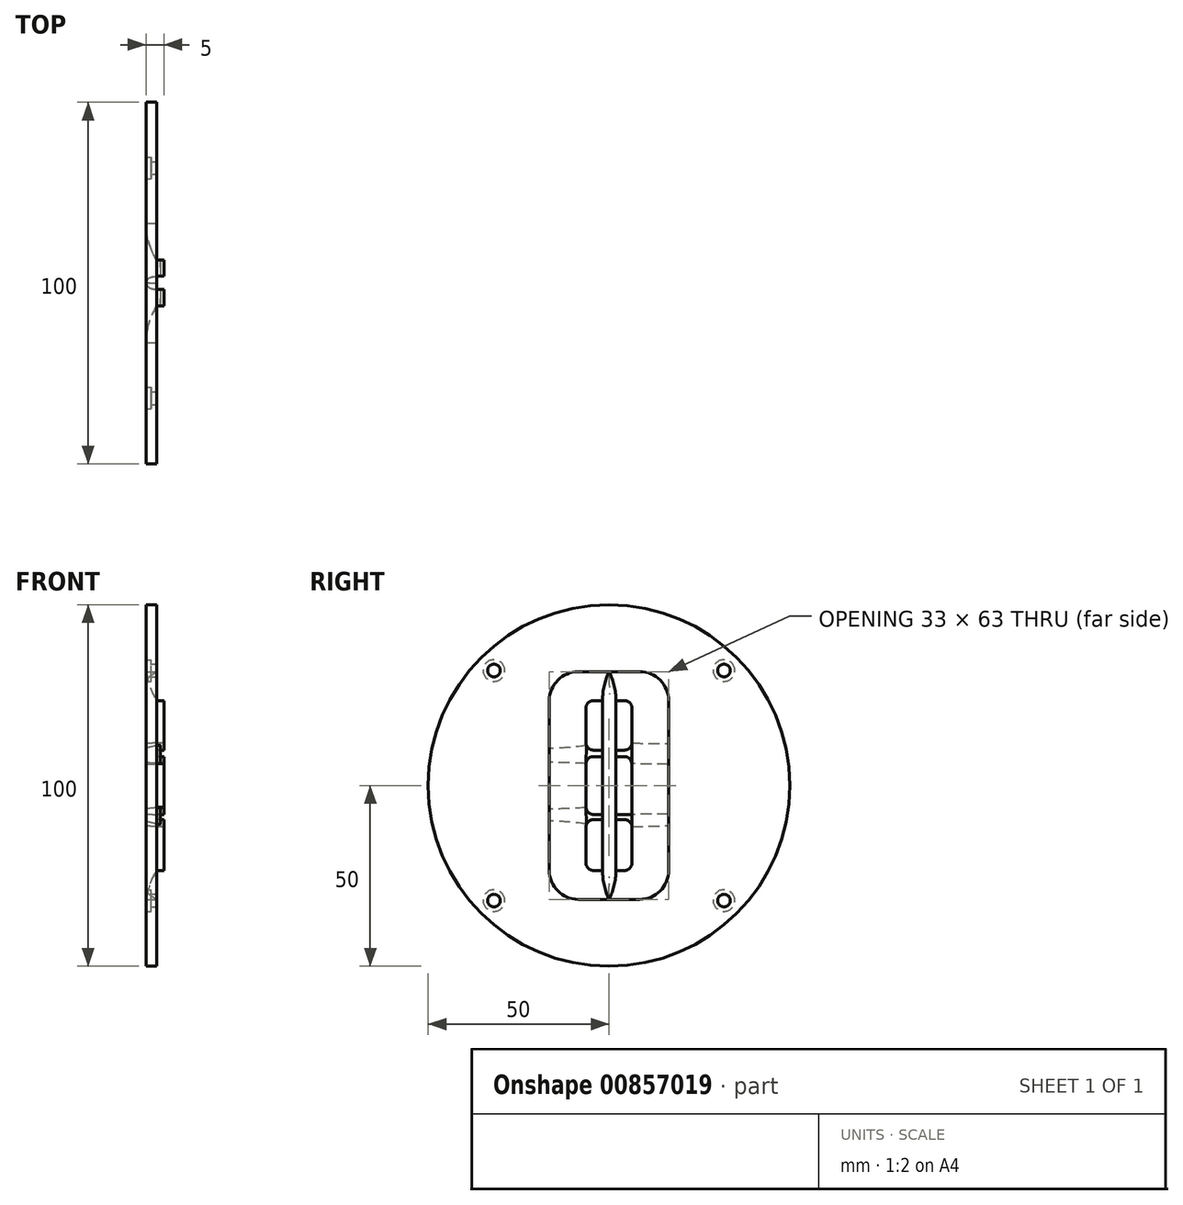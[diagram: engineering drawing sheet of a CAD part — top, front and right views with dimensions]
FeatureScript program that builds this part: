
annotation { "Feature Type Name" : "Feature", "Feature Type Description" : "" }
export const myFeature = defineFeature(function(context is Context, id is Id, definition is map)
    precondition{}
    {
        {
            var Q0;
            Q0=qCreatedBy(makeId("Right.planeOp"),FACE);
            var sketch = newSketch(context, id + "F0", { "sketchPlane" : qUnion([Q0])});
            skCircle(sketch, "E0", {"center": v(0, 0) * mm, "radius": 45 * mm});
            skCircle(sketch, "E1", {"center": v(0, 0) * mm, "radius": 50 * mm});
            skLineSegment(sketch, "E2", {"start": v(0, 0) * mm, "end": v(0, 58.72) * mm});
            skCircle(sketch, "E3", {"center": v(31.82, 31.82) * mm, "radius": 1.75 * mm});
            skCircle(sketch, "E4", {"center": v(31.82, 31.82) * mm, "radius": 3 * mm});
            skCircle(sketch, "E5.1.0", {"center": v(-31.82, 31.82) * mm, "radius": 3 * mm});
            skCircle(sketch, "E5.2.0", {"center": v(-31.82, -31.82) * mm, "radius": 3 * mm});
            skCircle(sketch, "E5.3.0", {"center": v(31.82, -31.82) * mm, "radius": 3 * mm});
            skCircle(sketch, "E6.1.0", {"center": v(-31.82, 31.82) * mm, "radius": 1.75 * mm});
            skCircle(sketch, "E6.2.0", {"center": v(-31.82, -31.82) * mm, "radius": 1.75 * mm});
            skCircle(sketch, "E6.3.0", {"center": v(31.82, -31.82) * mm, "radius": 1.75 * mm});
            skLineSegment(sketch, "E7", {"start": v(0, 0) * mm, "end": v(0, -59.24) * mm});
            skLineSegment(sketch, "E8.bottom", {"start": v(8.5, 31.5) * mm, "end": v(-8.5, 31.5) * mm});
            skLineSegment(sketch, "E8.top", {"start": v(8.5, -31.5) * mm, "end": v(-8.5, -31.5) * mm});
            skLineSegment(sketch, "E8.left", {"start": v(16.5, 23.5) * mm, "end": v(16.5, -23.5) * mm});
            skLineSegment(sketch, "E8.right", {"start": v(-16.5, 23.5) * mm, "end": v(-16.5, -23.5) * mm});
            skLineSegment(sketch, "E9.bottom", {"start": v(4.28, 8) * mm, "end": v(2.98, 8) * mm});
            skLineSegment(sketch, "E9.top", {"start": v(6.28, -8) * mm, "end": v(2.98, -8) * mm});
            skLineSegment(sketch, "E9.left", {"start": v(6.28, 6) * mm, "end": v(6.28, -8) * mm});
            skLineSegment(sketch, "E10.trimOffspring", {"start": v(29.7, 29.7) * mm, "end": v(45.9, 45.9) * mm});
            skPoint(sketch, "E11.orphan", {"position": v(2.98, -17) * mm});
            skPoint(sketch, "E12.visualSharp", {"position": v(16.5, 31.5) * mm});
            skArc(sketch, "E12.filletArc", {"start": v(16.5, 23.5) * mm, "mid": v(14.16, 29.16) * mm, "end": v(8.5, 31.5) * mm});
            skPoint(sketch, "E13.visualSharp", {"position": v(-16.5, -31.5) * mm});
            skArc(sketch, "E13.filletArc", {"start": v(-16.5, -23.5) * mm, "mid": v(-14.16, -29.16) * mm, "end": v(-8.5, -31.5) * mm});
            skPoint(sketch, "E14.visualSharp", {"position": v(-16.5, 31.5) * mm});
            skArc(sketch, "E14.filletArc", {"start": v(-8.5, 31.5) * mm, "mid": v(-14.16, 29.16) * mm, "end": v(-16.5, 23.5) * mm});
            skPoint(sketch, "E15.visualSharp", {"position": v(16.5, -31.5) * mm});
            skArc(sketch, "E15.filletArc", {"start": v(8.5, -31.5) * mm, "mid": v(14.16, -29.16) * mm, "end": v(16.5, -23.5) * mm});
            skLineSegment(sketch, "E16.bottom", {"start": v(4.35, 23.5) * mm, "end": v(1.93, 23.5) * mm});
            skLineSegment(sketch, "E16.top", {"start": v(4.35, -23.5) * mm, "end": v(1.93, -23.5) * mm});
            skLineSegment(sketch, "E16.left", {"start": v(6.35, 21.5) * mm, "end": v(6.35, 11.8) * mm});
            skLineSegment(sketch, "E16.right", {"start": v(-6.35, 21.5) * mm, "end": v(-6.35, 11.8) * mm});
            skLineSegment(sketch, "E17", {"start": v(1.93, 23.5) * mm, "end": v(1.93, -23.5) * mm});
            skLineSegment(sketch, "E18", {"start": v(-1.78, -23.5) * mm, "end": v(-1.78, 23.5) * mm});
            skLineSegment(sketch, "E19", {"start": v(4.35, 9.8) * mm, "end": v(1.93, 9.8) * mm});
            skLineSegment(sketch, "E20", {"start": v(2.98, 8) * mm, "end": v(1.93, 8) * mm});
            skLineSegment(sketch, "E21", {"start": v(6.28, -8) * mm, "end": v(1.93, -8) * mm});
            skLineSegment(sketch, "E22", {"start": v(4.35, -9.47) * mm, "end": v(1.93, -9.47) * mm});
            skArc(sketch, "E23", {"start": v(1.93, 23.5) * mm, "mid": v(1.44, 27.61) * mm, "end": v(0, 31.5) * mm});
            skArc(sketch, "E24", {"start": v(0, 31.5) * mm, "mid": v(-1.33, 27.6) * mm, "end": v(-1.78, 23.5) * mm});
            skArc(sketch, "E25", {"start": v(-1.78, -23.5) * mm, "mid": v(-1.33, -27.6) * mm, "end": v(0, -31.5) * mm});
            skArc(sketch, "E26", {"start": v(0, -31.5) * mm, "mid": v(1.44, -27.61) * mm, "end": v(1.93, -23.5) * mm});
            skPoint(sketch, "E27.visualSharp", {"position": v(6.35, -23.5) * mm});
            skArc(sketch, "E27.filletArc", {"start": v(4.35, -23.5) * mm, "mid": v(5.76, -22.91) * mm, "end": v(6.35, -21.5) * mm});
            skPoint(sketch, "E28.visualSharp", {"position": v(-6.35, -23.5) * mm});
            skArc(sketch, "E28.filletArc", {"start": v(-6.35, -21.5) * mm, "mid": v(-5.76, -22.91) * mm, "end": v(-4.35, -23.5) * mm});
            skPoint(sketch, "E29.visualSharp", {"position": v(-6.35, 23.5) * mm});
            skArc(sketch, "E29.filletArc", {"start": v(-4.35, 23.5) * mm, "mid": v(-5.76, 22.91) * mm, "end": v(-6.35, 21.5) * mm});
            skPoint(sketch, "E30.visualSharp", {"position": v(6.35, 23.5) * mm});
            skArc(sketch, "E30.filletArc", {"start": v(6.35, 21.5) * mm, "mid": v(5.76, 22.91) * mm, "end": v(4.35, 23.5) * mm});
            skLineSegment(sketch, "E31.trimOffspring", {"start": v(-6.35, 6) * mm, "end": v(-6.35, -6) * mm});
            skLineSegment(sketch, "E32.trimOffspring", {"start": v(-1.78, 8) * mm, "end": v(-4.35, 8) * mm});
            skLineSegment(sketch, "E33.trimOffspring", {"start": v(-1.78, 9.8) * mm, "end": v(-4.35, 9.8) * mm});
            skLineSegment(sketch, "E34.trimOffspring", {"start": v(6.35, -11.47) * mm, "end": v(6.35, -21.5) * mm});
            skLineSegment(sketch, "E35.trimOffspring", {"start": v(-1.78, 23.5) * mm, "end": v(-4.35, 23.5) * mm});
            skLineSegment(sketch, "E36.trimOffspring", {"start": v(-6.35, -11.47) * mm, "end": v(-6.35, -21.5) * mm});
            skLineSegment(sketch, "E37.trimOffspring", {"start": v(-1.78, -8) * mm, "end": v(-4.35, -8) * mm});
            skLineSegment(sketch, "E38.trimOffspring", {"start": v(-1.78, -9.47) * mm, "end": v(-4.35, -9.47) * mm});
            skLineSegment(sketch, "E39.trimOffspring", {"start": v(-1.78, -23.5) * mm, "end": v(-4.35, -23.5) * mm});
            skPoint(sketch, "E40.visualSharp", {"position": v(6.35, -9.47) * mm});
            skArc(sketch, "E40.filletArc", {"start": v(6.35, -11.47) * mm, "mid": v(5.76, -10.05) * mm, "end": v(4.35, -9.47) * mm});
            skPoint(sketch, "E41.visualSharp", {"position": v(6.28, 8) * mm});
            skArc(sketch, "E41.filletArc", {"start": v(6.28, 6) * mm, "mid": v(5.7, 7.41) * mm, "end": v(4.28, 8) * mm});
            skPoint(sketch, "E42.visualSharp", {"position": v(-6.35, 8) * mm});
            skArc(sketch, "E42.filletArc", {"start": v(-4.35, 8) * mm, "mid": v(-5.76, 7.41) * mm, "end": v(-6.35, 6) * mm});
            skPoint(sketch, "E43.visualSharp", {"position": v(6.35, 9.8) * mm});
            skArc(sketch, "E43.filletArc", {"start": v(4.35, 9.8) * mm, "mid": v(5.76, 10.39) * mm, "end": v(6.35, 11.8) * mm});
            skPoint(sketch, "E44.visualSharp", {"position": v(-6.35, 9.8) * mm});
            skArc(sketch, "E44.filletArc", {"start": v(-6.35, 11.8) * mm, "mid": v(-5.76, 10.39) * mm, "end": v(-4.35, 9.8) * mm});
            skPoint(sketch, "E45.visualSharp", {"position": v(-6.35, -9.47) * mm});
            skArc(sketch, "E45.filletArc", {"start": v(-4.35, -9.47) * mm, "mid": v(-5.76, -10.05) * mm, "end": v(-6.35, -11.47) * mm});
            skPoint(sketch, "E46.visualSharp", {"position": v(-6.35, -8) * mm});
            skArc(sketch, "E46.filletArc", {"start": v(-6.35, -6) * mm, "mid": v(-5.76, -7.41) * mm, "end": v(-4.35, -8) * mm});
            skLineSegment(sketch, "E47", {"start": v(6.35, 11.8) * mm, "end": v(6.28, 6) * mm});
            skLineSegment(sketch, "E48", {"start": v(-6.22, 11.09) * mm, "end": v(-6.35, 6) * mm});
            skLineSegment(sketch, "E49", {"start": v(6.28, -8) * mm, "end": v(6.35, -11.47) * mm});
            skLineSegment(sketch, "E50", {"start": v(-6.35, -6) * mm, "end": v(-6.2, -10.68) * mm});
            skSolve(sketch);
        }
        {
            var Q0;
            {var subQ0=sQuery(id+"F0.wireOp",EDGE,"E4");var subQ1=sQuery(id+"F0.wireOp",EDGE,"E0");var subQ2=makeQuery(id+"F0.imprint","INTERSECT",VERTEX,{"disambiguationData":[OD(1.0)],"derivedFrom":[subQ1,subQ0]});Q0=makeQuery(id+"F0.imprint","IMPRINT",FACE,{"disambiguationData":[TD([[makeQuery(id+"F0.imprint","IMPRINT",EDGE,{"disambiguationData":[TD([[subQ2,-1.0]])],"derivedFrom":subQ1}),-1.0]])]});}
            var Q1;
            {var subQ1=sQuery(id+"F0.wireOp",EDGE,"E0");var subQ7=sQuery(id+"F0.wireOp",EDGE,"E7");var subQ11=makeQuery(id+"F0.imprint","INTERSECT",VERTEX,{"derivedFrom":[subQ1,subQ7]});Q1=makeQuery(id+"F0.imprint","IMPRINT",FACE,{"disambiguationData":[TD([[makeQuery(id+"F0.imprint","IMPRINT",EDGE,{"disambiguationData":[TD([[subQ11,-1.0]])],"derivedFrom":subQ1}),-1.0]])]});}
            var Q2;
            Q2=makeQuery(id+"F0.imprint","IMPRINT",FACE,{"disambiguationData":[TD([[makeQuery(id+"F0.imprint","IMPRINT",EDGE,{"derivedFrom":sQuery(id+"F0.wireOp",EDGE,"E8.left")}),1.0]])]});
            var Q3;
            {var subQ1=sQuery(id+"F0.wireOp",EDGE,"E0");var subQ5=sQuery(id+"F0.wireOp",EDGE,"E2");var subQ8=makeQuery(id+"F0.imprint","INTERSECT",VERTEX,{"derivedFrom":[subQ1,subQ5]});Q3=makeQuery(id+"F0.imprint","IMPRINT",FACE,{"disambiguationData":[TD([[makeQuery(id+"F0.imprint","IMPRINT",EDGE,{"disambiguationData":[TD([[subQ8,-1.0]])],"derivedFrom":subQ1}),-1.0]])]});}
            var Q4;
            Q4=makeQuery(id+"F0.imprint","IMPRINT",FACE,{"disambiguationData":[TD([[makeQuery(id+"F0.imprint","IMPRINT",EDGE,{"derivedFrom":sQuery(id+"F0.wireOp",EDGE,"E8.right")}),-1.0]])]});
            extrude(context, id + "F1", {"entities" : qUnion([Q0, Q1, Q2, Q3, Q4]), "oppositeDirection" : true, "depth" : 3 * mm, "offsetDistance" : 25 * mm});
        }
        {
            var Q0;
            Q0=makeQuery(id+"F0.imprint","IMPRINT",FACE,{"disambiguationData":[TD([[makeQuery(id+"F0.imprint","IMPRINT",EDGE,{"derivedFrom":sQuery(id+"F0.wireOp",EDGE,"E9.bottom")}),-1.0]])]});
            var Q1;
            {var subQ1=sQuery(id+"F0.wireOp",EDGE,"E32.trimOffspring");Q1=makeQuery(id+"F0.imprint","IMPRINT",FACE,{"disambiguationData":[TD([[makeQuery(id+"F0.imprint","IMPRINT",EDGE,{"derivedFrom":subQ1}),-1.0]])]});}
            var Q2;
            {var subQ4=sQuery(id+"F0.wireOp",EDGE,"E37.trimOffspring");Q2=makeQuery(id+"F0.imprint","IMPRINT",FACE,{"disambiguationData":[TD([[makeQuery(id+"F0.imprint","IMPRINT",EDGE,{"derivedFrom":subQ4}),1.0]])]});}
            var Q3;
            {var subQ0=sQuery(id+"F0.wireOp",EDGE,"E22");Q3=makeQuery(id+"F0.imprint","IMPRINT",FACE,{"disambiguationData":[TD([[makeQuery(id+"F0.imprint","IMPRINT",EDGE,{"derivedFrom":subQ0}),-1.0]])]});}
            extrude(context, id + "F2", {"entities" : qUnion([Q0, Q1, Q2, Q3]), "depth" : 1 * mm, "offsetDistance" : 25 * mm});
        }
        {
            var Q0;
            {var subQ0=sQuery(id+"F0.wireOp",EDGE,"E23");Q0=makeQuery(id+"F0.imprint","IMPRINT",FACE,{"disambiguationData":[TD([[makeQuery(id+"F0.imprint","IMPRINT",EDGE,{"derivedFrom":subQ0}),1.0]])]});}
            var Q1;
            {var subQ3=sQuery(id+"F0.wireOp",EDGE,"E24");Q1=makeQuery(id+"F0.imprint","IMPRINT",FACE,{"disambiguationData":[TD([[makeQuery(id+"F0.imprint","IMPRINT",EDGE,{"derivedFrom":subQ3}),1.0]])]});}
            extrude(context, id + "F3", {"entities" : qUnion([Q0, Q1]), "oppositeDirection" : true, "depth" : 3 * mm, "offsetDistance" : 25 * mm, "hasDraft" : true, "draftAngle" : 15 * degree, "draftPullDirection" : true});
        }
        {
            var Q0;
            Q0=makeQuery(id+"F3.opExtrude","CAP_EDGE",EDGE,{"disambiguationData":[OSD([sQuery(id+"F0.wireOp",EDGE,"E17")])],"isStart":false});
            var Q1;
            Q1=makeQuery(id+"F3.opExtrude","CAP_EDGE",EDGE,{"disambiguationData":[OSD([sQuery(id+"F0.wireOp",EDGE,"E18")])],"isStart":false});
            fillet(context, id + "F4", {"entities" : qUnion([Q0, Q1]), "radius" : 1.25 * mm, "tangentPropagation" : true, "allowEdgeOverflow" : false});
        }
        {
            var Q0;
            Q0=makeQuery(id+"F0.imprint","IMPRINT",FACE,{"disambiguationData":[TD([[makeQuery(id+"F0.imprint","IMPRINT",EDGE,{"derivedFrom":sQuery(id+"F0.wireOp",EDGE,"E8.left")}),-1.0]])]});
            var Q1;
            Q1=makeQuery(id+"F0.imprint","IMPRINT",FACE,{"disambiguationData":[TD([[makeQuery(id+"F0.imprint","IMPRINT",EDGE,{"derivedFrom":sQuery(id+"F0.wireOp",EDGE,"E8.right")}),1.0]])]});
            extrude(context, id + "F5", {"entities" : qUnion([Q0, Q1]), "oppositeDirection" : true, "depth" : 3 * mm, "offsetDistance" : 25 * mm});
        }
        {
            var Q0;
            Q0=makeQuery(id+"F5.opExtrude","CAP_EDGE",EDGE,{"disambiguationData":[OSD([sQuery(id+"F0.wireOp",EDGE,"E31.trimOffspring")])],"isStart":false});
            var Q1;
            Q1=makeQuery(id+"F5.opExtrude","CAP_EDGE",EDGE,{"disambiguationData":[OSD([sQuery(id+"F0.wireOp",EDGE,"E36.trimOffspring")])],"isStart":false});
            var Q2;
            Q2=makeQuery(id+"F5.opExtrude","CAP_EDGE",EDGE,{"disambiguationData":[OSD([sQuery(id+"F0.wireOp",EDGE,"E16.right")])],"isStart":false});
            var Q3;
            Q3=makeQuery(id+"F5.opExtrude","CAP_EDGE",EDGE,{"disambiguationData":[OSD([sQuery(id+"F0.wireOp",EDGE,"E9.left")])],"isStart":false});
            var Q4;
            Q4=makeQuery(id+"F5.opExtrude","CAP_EDGE",EDGE,{"disambiguationData":[OSD([sQuery(id+"F0.wireOp",EDGE,"E16.left")])],"isStart":false});
            var Q5;
            Q5=makeQuery(id+"F5.opExtrude","CAP_EDGE",EDGE,{"disambiguationData":[OSD([sQuery(id+"F0.wireOp",EDGE,"E34.trimOffspring")])],"isStart":false});
            fillet(context, id + "F6", {"entities" : qUnion([Q0, Q1, Q2, Q3, Q4, Q5]), "radius" : 18.5 * mm, "tangentPropagation" : true, "allowEdgeOverflow" : false});
        }
        {
            var Q0;
            Q0=qSketchRegion(id+"F0",true);
            var Q1;
            {var subQ0=sQuery(id+"F0.wireOp",EDGE,"E5.1.0");var subQ1=sQuery(id+"F0.wireOp",EDGE,"E0");var subQ2=makeQuery(id+"F0.imprint","INTERSECT",VERTEX,{"disambiguationData":[OD(0.0)],"derivedFrom":[subQ1,subQ0]});Q1=makeQuery(id+"F0.imprint","IMPRINT",FACE,{"disambiguationData":[TD([[makeQuery(id+"F0.imprint","IMPRINT",EDGE,{"disambiguationData":[TD([[subQ2,-1.0]])],"derivedFrom":subQ1}),1.0]])]});}
            var Q2;
            {var subQ0=sQuery(id+"F0.wireOp",EDGE,"E5.2.0");var subQ1=sQuery(id+"F0.wireOp",EDGE,"E0");var subQ2=makeQuery(id+"F0.imprint","INTERSECT",VERTEX,{"disambiguationData":[OD(0.0)],"derivedFrom":[subQ1,subQ0]});Q2=makeQuery(id+"F0.imprint","IMPRINT",FACE,{"disambiguationData":[TD([[makeQuery(id+"F0.imprint","IMPRINT",EDGE,{"disambiguationData":[TD([[subQ2,-1.0]])],"derivedFrom":subQ1}),-1.0]])]});}
            var Q3;
            {var subQ0=sQuery(id+"F0.wireOp",EDGE,"E5.2.0");var subQ1=sQuery(id+"F0.wireOp",EDGE,"E0");var subQ2=makeQuery(id+"F0.imprint","INTERSECT",VERTEX,{"disambiguationData":[OD(0.0)],"derivedFrom":[subQ1,subQ0]});Q3=makeQuery(id+"F0.imprint","IMPRINT",FACE,{"disambiguationData":[TD([[makeQuery(id+"F0.imprint","IMPRINT",EDGE,{"disambiguationData":[TD([[subQ2,-1.0]])],"derivedFrom":subQ1}),1.0]])]});}
            var Q4;
            {var subQ0=sQuery(id+"F0.wireOp",EDGE,"E5.3.0");var subQ1=sQuery(id+"F0.wireOp",EDGE,"E0");var subQ2=makeQuery(id+"F0.imprint","INTERSECT",VERTEX,{"disambiguationData":[OD(0.0)],"derivedFrom":[subQ1,subQ0]});Q4=makeQuery(id+"F0.imprint","IMPRINT",FACE,{"disambiguationData":[TD([[makeQuery(id+"F0.imprint","IMPRINT",EDGE,{"disambiguationData":[TD([[subQ2,-1.0]])],"derivedFrom":subQ1}),-1.0]])]});}
            var Q5;
            {var subQ0=sQuery(id+"F0.wireOp",EDGE,"E5.3.0");var subQ1=sQuery(id+"F0.wireOp",EDGE,"E0");var subQ2=makeQuery(id+"F0.imprint","INTERSECT",VERTEX,{"disambiguationData":[OD(0.0)],"derivedFrom":[subQ1,subQ0]});Q5=makeQuery(id+"F0.imprint","IMPRINT",FACE,{"disambiguationData":[TD([[makeQuery(id+"F0.imprint","IMPRINT",EDGE,{"disambiguationData":[TD([[subQ2,-1.0]])],"derivedFrom":subQ1}),1.0]])]});}
            var Q6;
            {var subQ0=sQuery(id+"F0.wireOp",EDGE,"E3");var subQ1=sQuery(id+"F0.wireOp",EDGE,"E0");var subQ2=makeQuery(id+"F0.imprint","INTERSECT",VERTEX,{"disambiguationData":[OD(0.0)],"derivedFrom":[subQ1,subQ0]});Q6=makeQuery(id+"F0.imprint","IMPRINT",FACE,{"disambiguationData":[TD([[makeQuery(id+"F0.imprint","IMPRINT",EDGE,{"disambiguationData":[TD([[subQ2,1.0]])],"derivedFrom":subQ1}),1.0]])]});}
            var Q7;
            {var subQ0=sQuery(id+"F0.wireOp",EDGE,"E3");var subQ1=sQuery(id+"F0.wireOp",EDGE,"E0");var subQ2=makeQuery(id+"F0.imprint","INTERSECT",VERTEX,{"disambiguationData":[OD(1.0)],"derivedFrom":[subQ1,subQ0]});Q7=makeQuery(id+"F0.imprint","IMPRINT",FACE,{"disambiguationData":[TD([[makeQuery(id+"F0.imprint","IMPRINT",EDGE,{"disambiguationData":[TD([[subQ2,-1.0]])],"derivedFrom":subQ1}),1.0]])]});}
            var Q8;
            {var subQ0=sQuery(id+"F0.wireOp",EDGE,"E3");var subQ1=sQuery(id+"F0.wireOp",EDGE,"E0");var subQ2=makeQuery(id+"F0.imprint","INTERSECT",VERTEX,{"disambiguationData":[OD(1.0)],"derivedFrom":[subQ1,subQ0]});Q8=makeQuery(id+"F0.imprint","IMPRINT",FACE,{"disambiguationData":[TD([[makeQuery(id+"F0.imprint","IMPRINT",EDGE,{"disambiguationData":[TD([[subQ2,-1.0]])],"derivedFrom":subQ1}),-1.0]])]});}
            var Q9;
            {var subQ0=sQuery(id+"F0.wireOp",EDGE,"E3");var subQ1=sQuery(id+"F0.wireOp",EDGE,"E0");var subQ2=makeQuery(id+"F0.imprint","INTERSECT",VERTEX,{"disambiguationData":[OD(0.0)],"derivedFrom":[subQ1,subQ0]});Q9=makeQuery(id+"F0.imprint","IMPRINT",FACE,{"disambiguationData":[TD([[makeQuery(id+"F0.imprint","IMPRINT",EDGE,{"disambiguationData":[TD([[subQ2,1.0]])],"derivedFrom":subQ1}),-1.0]])]});}
            var Q10;
            {var subQ0=sQuery(id+"F0.wireOp",EDGE,"E5.1.0");var subQ1=sQuery(id+"F0.wireOp",EDGE,"E0");var subQ2=makeQuery(id+"F0.imprint","INTERSECT",VERTEX,{"disambiguationData":[OD(0.0)],"derivedFrom":[subQ1,subQ0]});Q10=makeQuery(id+"F0.imprint","IMPRINT",FACE,{"disambiguationData":[TD([[makeQuery(id+"F0.imprint","IMPRINT",EDGE,{"disambiguationData":[TD([[subQ2,-1.0]])],"derivedFrom":subQ1}),-1.0]])]});}
            extrude(context, id + "F7", {"entities" : qUnion([Q0, Q1, Q2, Q3, Q4, Q5, Q6, Q7, Q8, Q9, Q10]), "operationType" : NewBodyOperationType.ADD, "oppositeDirection" : true, "depth" : 1.5 * mm, "offsetDistance" : 25 * mm});
        }
        {
            var Q0;
            {var subQ2=sQuery(id+"F0.wireOp",EDGE,"E16.bottom");Q0=makeQuery(id+"F0.imprint","IMPRINT",FACE,{"disambiguationData":[TD([[makeQuery(id+"F0.imprint","IMPRINT",EDGE,{"derivedFrom":subQ2}),1.0]])]});}
            var Q1;
            {var subQ1=sQuery(id+"F0.wireOp",EDGE,"E16.right");Q1=makeQuery(id+"F0.imprint","IMPRINT",FACE,{"disambiguationData":[TD([[makeQuery(id+"F0.imprint","IMPRINT",EDGE,{"derivedFrom":subQ1}),1.0]])]});}
            var Q2;
            {var subQ6=sQuery(id+"F0.wireOp",EDGE,"E31.trimOffspring");Q2=makeQuery(id+"F0.imprint","IMPRINT",FACE,{"disambiguationData":[TD([[makeQuery(id+"F0.imprint","IMPRINT",EDGE,{"derivedFrom":subQ6}),1.0]])]});}
            var Q3;
            Q3=makeQuery(id+"F0.imprint","IMPRINT",FACE,{"disambiguationData":[TD([[makeQuery(id+"F0.imprint","IMPRINT",EDGE,{"derivedFrom":sQuery(id+"F0.wireOp",EDGE,"E9.bottom")}),1.0]])]});
            var Q4;
            {var subQ0=sQuery(id+"F0.wireOp",EDGE,"E16.top");Q4=makeQuery(id+"F0.imprint","IMPRINT",FACE,{"disambiguationData":[TD([[makeQuery(id+"F0.imprint","IMPRINT",EDGE,{"derivedFrom":subQ0}),-1.0]])]});}
            var Q5;
            Q5=makeQuery(id+"F0.imprint","IMPRINT",FACE,{"disambiguationData":[TD([[makeQuery(id+"F0.imprint","IMPRINT",EDGE,{"derivedFrom":sQuery(id+"F0.wireOp",EDGE,"E28.filletArc")}),1.0]])]});
            extrude(context, id + "F8", {"entities" : qUnion([Q0, Q1, Q2, Q3, Q4, Q5]), "depth" : 2 * mm, "offsetDistance" : 25 * mm});
        }
    });
